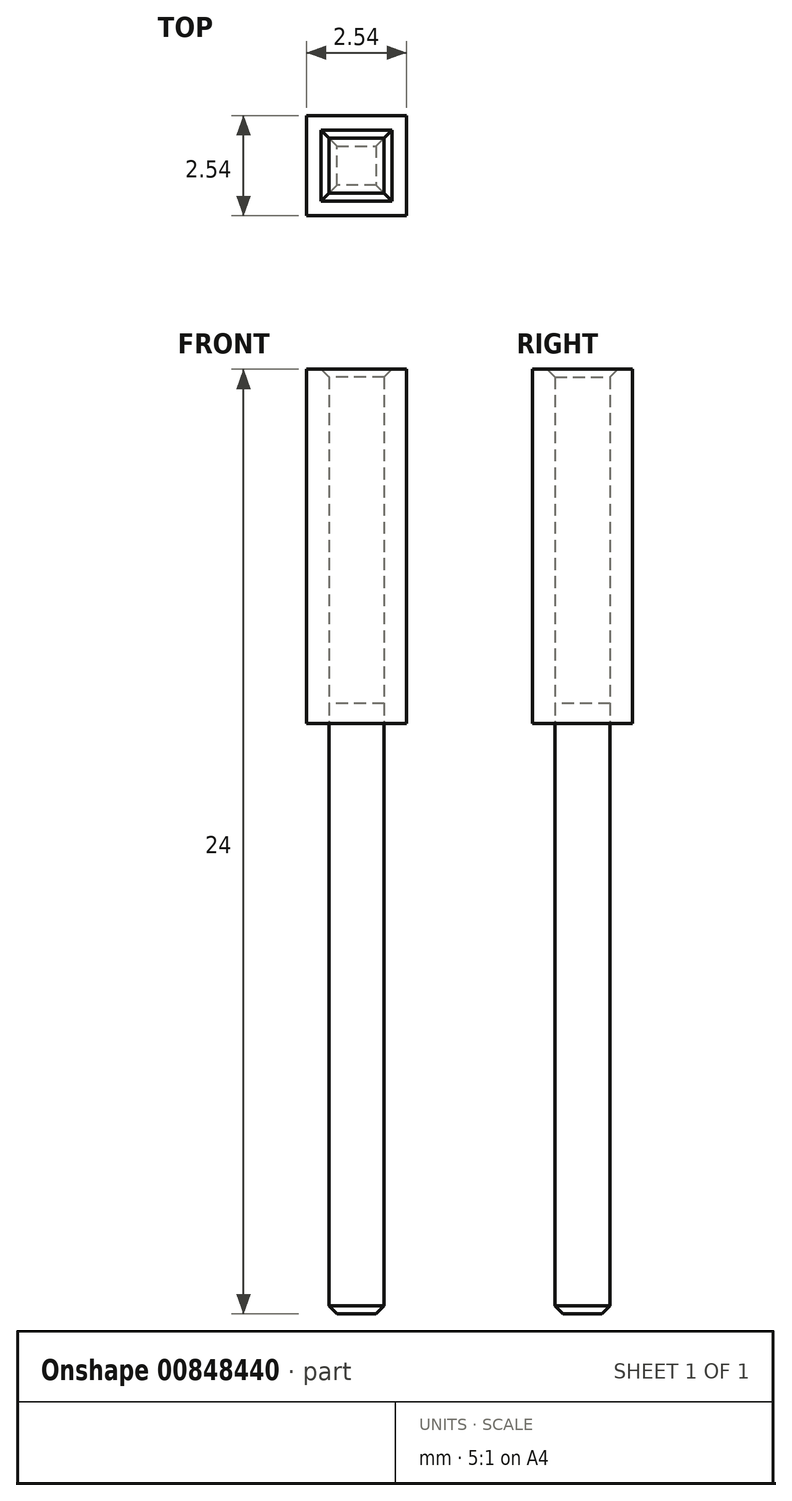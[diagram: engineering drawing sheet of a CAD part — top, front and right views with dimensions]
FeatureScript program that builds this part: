
annotation { "Feature Type Name" : "Feature", "Feature Type Description" : "" }
export const myFeature = defineFeature(function(context is Context, id is Id, definition is map)
    precondition{}
    {
        {
            var Q0;
            Q0=qCreatedBy(makeId("Top.planeOp"),FACE);
            var sketch = newSketch(context, id + "F0", { "sketchPlane" : qUnion([Q0])});
            skLineSegment(sketch, "E0.bottom", {"start": v(1.27, 1.27) * mm, "end": v(-1.27, 1.27) * mm});
            skLineSegment(sketch, "E0.top", {"start": v(1.27, -1.27) * mm, "end": v(-1.27, -1.27) * mm});
            skLineSegment(sketch, "E0.left", {"start": v(1.27, 1.27) * mm, "end": v(1.27, -1.27) * mm});
            skLineSegment(sketch, "E0.right", {"start": v(-1.27, 1.27) * mm, "end": v(-1.27, -1.27) * mm});
            skPoint(sketch, "E0.middle", {"position": v(0, 0) * mm});
            skLineSegment(sketch, "E1.bottom", {"start": v(0.7, 0.7) * mm, "end": v(-0.7, 0.7) * mm});
            skLineSegment(sketch, "E1.top", {"start": v(0.7, -0.7) * mm, "end": v(-0.7, -0.7) * mm});
            skLineSegment(sketch, "E1.left", {"start": v(0.7, 0.7) * mm, "end": v(0.7, -0.7) * mm});
            skLineSegment(sketch, "E1.right", {"start": v(-0.7, 0.7) * mm, "end": v(-0.7, -0.7) * mm});
            skSolve(sketch);
        }
        {
            var Q0;
            Q0 = qSketchRegion(id + "F0", true);
            extrude(context, id + "F1", {"entities" : qUnion([Q0]), "depth" : 9 * mm, "offsetDistance" : 25 * mm});
        }
        {
            var Q0;
            Q0=makeQuery(id+"F1.opExtrude","CAP_EDGE",EDGE,{"disambiguationData":[OSD([sQuery(id+"F0.wireOp",EDGE,"E1.top")])],"isStart":false});
            var Q1;
            Q1=makeQuery(id+"F1.opExtrude","CAP_EDGE",EDGE,{"disambiguationData":[OSD([sQuery(id+"F0.wireOp",EDGE,"E1.right")])],"isStart":false});
            var Q2;
            Q2=makeQuery(id+"F1.opExtrude","CAP_EDGE",EDGE,{"disambiguationData":[OSD([sQuery(id+"F0.wireOp",EDGE,"E1.bottom")])],"isStart":false});
            var Q3;
            Q3=makeQuery(id+"F1.opExtrude","CAP_EDGE",EDGE,{"disambiguationData":[OSD([sQuery(id+"F0.wireOp",EDGE,"E1.left")])],"isStart":false});
            chamfer(context, id + "F2", {"entities" : qUnion([Q0, Q1, Q2, Q3]), "width" : 0.2 * mm, "tangentPropagation" : true});
        }
        {
            var Q0;
            Q0=makeQuery(id+"F1.opExtrude","CAP_FACE",FACE,{"disambiguationData":[OSD([sQuery(id+"F0.wireOp",EDGE,"E0.bottom"),sQuery(id+"F0.wireOp",EDGE,"E0.top"),sQuery(id+"F0.wireOp",EDGE,"E0.left"),sQuery(id+"F0.wireOp",EDGE,"E0.right"),sQuery(id+"F0.wireOp",EDGE,"E1.bottom"),sQuery(id+"F0.wireOp",EDGE,"E1.top"),sQuery(id+"F0.wireOp",EDGE,"E1.left"),sQuery(id+"F0.wireOp",EDGE,"E1.right")])],"isStart":true});
            var sketch = newSketch(context, id + "F3", { "sketchPlane" : qUnion([Q0])});
            skLineSegment(sketch, "E2.bottom", {"start": v(0.7, 0.7) * mm, "end": v(-0.7, 0.7) * mm});
            skLineSegment(sketch, "E2.top", {"start": v(0.7, -0.7) * mm, "end": v(-0.7, -0.7) * mm});
            skLineSegment(sketch, "E2.left", {"start": v(0.7, 0.7) * mm, "end": v(0.7, -0.7) * mm});
            skLineSegment(sketch, "E2.right", {"start": v(-0.7, 0.7) * mm, "end": v(-0.7, -0.7) * mm});
            skPoint(sketch, "E2.middle", {"position": v(0, 0) * mm});
            skSolve(sketch);
        }
        {
            var Q0;
            Q0=makeQuery(id+"F3.imprint","IMPRINT",FACE,{"disambiguationData":[TD([[makeQuery(id+"F3.imprint","IMPRINT",EDGE,{"derivedFrom":sQuery(id+"F3.wireOp",EDGE,"E2.bottom")}),1.0]])]});
            extrude(context, id + "F4", {"entities" : qUnion([Q0]), "depth" : 15 * mm, "offsetDistance" : 25 * mm});
        }
        {
            var Q0;
            Q0=makeQuery(id+"F4.opExtrude","CAP_EDGE",EDGE,{"disambiguationData":[OSD([sQuery(id+"F3.wireOp",EDGE,"E2.right")])],"isStart":false});
            var Q1;
            Q1=makeQuery(id+"F4.opExtrude","CAP_EDGE",EDGE,{"disambiguationData":[OSD([sQuery(id+"F3.wireOp",EDGE,"E2.top")])],"isStart":false});
            var Q2;
            Q2=makeQuery(id+"F4.opExtrude","CAP_EDGE",EDGE,{"disambiguationData":[OSD([sQuery(id+"F3.wireOp",EDGE,"E2.left")])],"isStart":false});
            var Q3;
            Q3=makeQuery(id+"F4.opExtrude","CAP_EDGE",EDGE,{"disambiguationData":[OSD([sQuery(id+"F3.wireOp",EDGE,"E2.bottom")])],"isStart":false});
            chamfer(context, id + "F5", {"entities" : qUnion([Q0, Q1, Q2, Q3]), "width" : 0.2 * mm, "tangentPropagation" : true});
        }
        {
            var Q0;
            Q0=makeQuery(id+"F4.opExtrude","CAP_FACE",FACE,{"disambiguationData":[OSD([sQuery(id+"F3.wireOp",EDGE,"E2.bottom"),sQuery(id+"F3.wireOp",EDGE,"E2.top"),sQuery(id+"F3.wireOp",EDGE,"E2.left"),sQuery(id+"F3.wireOp",EDGE,"E2.right")])],"isStart":true});
            extrude(context, id + "F6", {"entities" : qUnion([Q0]), "depth" : 0.5 * mm, "offsetDistance" : 25 * mm});
        }
    });
